# Revit family: Doors_Garage_Asta-America_700-Series
name_source: partatom
category: Doors
units: mm (PartAtom-declared; Revit-internal decimal feet)

## family parameters
Always vertical = Yes
Cut with Voids When Loaded = No
Host = Wall
OmniClass Number = 23.30.10.17.27.11
Room Calculation Point = No
Shared = No

## types (4) — shared parameters
Analytic Construction = <None>
Assembly Code = B2030400
Bottom Bar = Asta America - Steel
Crank Visibility Left = No
Curtain Slats = Asta America - Steel - Powder Coat - Grey Topcoat
Description = ASTA AMERICA 700 Series Counter Shutters
Edition number = 1
Guides = Asta America - Steel
Height MAX = 10' - 0"
Hood = Asta America - Steel - Galvanized
Keynote = 08110
Manufacturer = Asta America
Model = 700 Series Insulated Service Doors
Product Guid = 7ab2d277-27dc-4f61-9033-bd4a7568a898
Product data url = https://www.bimobject.com
Slat Height = 0' - 2 21/256"
URL = www.astaamerica.com
Wall Closure = By host
Width MAX = 14' - 0"
wPanels = No

## per-type parameters (varying)
| type | Between Jambs | Crank Visibility Right | Face of Wall | Guide Height | Height | Height Control | No of Curtain Slats | Opening Height | Opening Width | Part Slat Number | Rough Height | Slat Distance | Width | _Clearance_height |
| Between Jamb with crank with handle | Yes | Yes | No | 5' - 0" | 5' - 0" | 5' - 0" | 29 | 5' - 0" | 6' - 7 1/2" | 27 | 5' - 10" | 0' - 5 229/256" | 7' - 0" | 5' - 10" |
| Between Jamb with turbular motor | Yes | No | No | 5' - 0" | 5' - 0" | 5' - 0" | 29 | 5' - 0" | 6' - 7 1/2" | 27 | 5' - 10" | 0' - 5 229/256" | 7' - 0" | 5' - 10" |
| Face of Wall with crank with handle | No | Yes | Yes | 10' - 0" | 12' - 0" | 10' - 0" | 58 | 12' - 0" | 16' - 0" | 56 | 10' - 0" | 0' - 0" | 16' - 4 1/2" | 10' - 10" |
| Face of Wall with turbular motor | No | No | Yes | 5' - 0" | 5' - 0" | 5' - 0" | 29 | 5' - 0" | 6' - 7 1/2" | 27 | 5' - 0" | 0' - 0" | 7' - 0" | 5' - 10" |

## geometry (parser evidence)
native form markers: Sweep x15
no freeform markers — native parametric forms only
